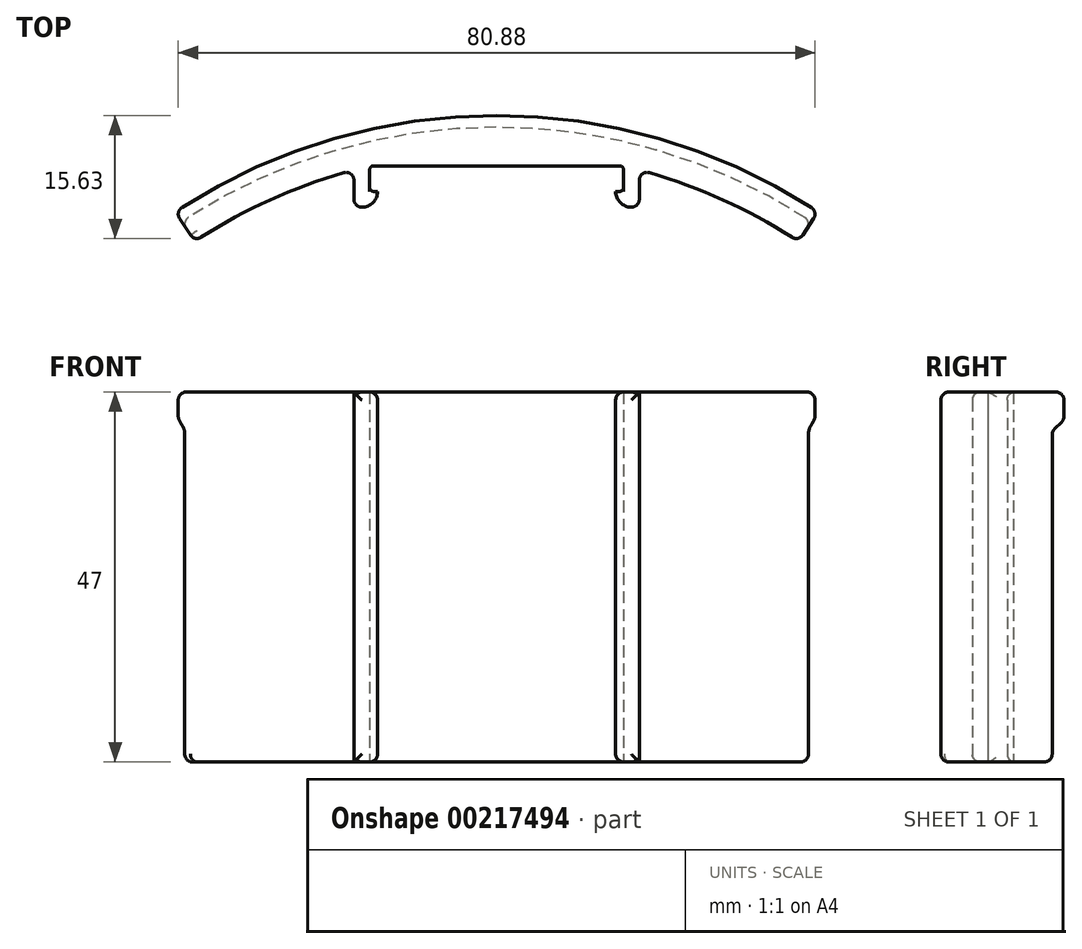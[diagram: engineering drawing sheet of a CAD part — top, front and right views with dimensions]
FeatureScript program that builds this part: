
annotation { "Feature Type Name" : "Feature", "Feature Type Description" : "" }
export const myFeature = defineFeature(function(context is Context, id is Id, definition is map)
    precondition{}
    {
        {
            var Q0;
            Q0=qCreatedBy(makeId("Top.planeOp"),FACE);
            var sketch = newSketch(context, id + "F0", { "sketchPlane" : qUnion([Q0])});
            skArc(sketch, "E0", {"start": v(40, 0) * mm, "mid": v(0, 12) * mm, "end": v(-40, 0) * mm});
            skPoint(sketch, "E1", {"position": v(0, 12) * mm});
            skArc(sketch, "E2.0", {"start": v(38.35, -2.5) * mm, "mid": v(0, 9) * mm, "end": v(-38.35, -2.5) * mm});
            skLineSegment(sketch, "E3", {"start": v(-40, 0) * mm, "end": v(-38.35, -2.5) * mm});
            skLineSegment(sketch, "E4", {"start": v(40, 0) * mm, "end": v(38.35, -2.5) * mm});
            skLineSegment(sketch, "E5", {"start": v(-16.12, 7.1) * mm, "end": v(16.12, 7.1) * mm});
            skLineSegment(sketch, "E6", {"start": v(-16.12, 7.1) * mm, "end": v(-16.12, 3.86) * mm});
            skLineSegment(sketch, "E7", {"start": v(-16.12, 3.86) * mm, "end": v(-15.12, 3.86) * mm});
            skLineSegment(sketch, "E8", {"start": v(-15.12, 3.86) * mm, "end": v(-15.12, 3.86) * mm});
            skLineSegment(sketch, "E9", {"start": v(-17.12, 1.86) * mm, "end": v(-18.13, 1.86) * mm});
            skLineSegment(sketch, "E10", {"start": v(-18.13, 1.86) * mm, "end": v(-18.13, 6.6) * mm});
            skLineSegment(sketch, "E11.MirrorCS", {"start": v(18.13, 1.86) * mm, "end": v(18.13, 6.6) * mm});
            skLineSegment(sketch, "E12.MirrorCS", {"start": v(16.12, 7.1) * mm, "end": v(16.12, 3.86) * mm});
            skLineSegment(sketch, "E13.MirrorCS", {"start": v(17.12, 1.86) * mm, "end": v(18.13, 1.86) * mm});
            skLineSegment(sketch, "E14.MirrorCS", {"start": v(16.12, 3.86) * mm, "end": v(15.12, 3.86) * mm});
            skLineSegment(sketch, "E15.MirrorCS", {"start": v(15.12, 3.86) * mm, "end": v(15.12, 3.86) * mm});
            skPoint(sketch, "E16.visualSharp", {"position": v(-15.12, 1.86) * mm});
            skArc(sketch, "E16.filletArc", {"start": v(-17.12, 1.86) * mm, "mid": v(-15.71, 2.44) * mm, "end": v(-15.13, 3.86) * mm});
            skPoint(sketch, "E17.visualSharp", {"position": v(15.12, 1.86) * mm});
            skArc(sketch, "E17.filletArc", {"start": v(15.13, 3.86) * mm, "mid": v(15.71, 2.44) * mm, "end": v(17.12, 1.86) * mm});
            skSolve(sketch);
        }
        {
            var Q0;
            Q0 = qSketchRegion(id + "F0", true);
            extrude(context, id + "F1", {"entities" : qUnion([Q0]), "endBound" : BoundingType.SYMMETRIC, "depth" : 47 * mm, "hasSecondDirection" : true, "secondDirectionOppositeDirection" : true, "secondDirectionDepth" : 25 * mm});
        }
        {
            var Q0;
            Q0=makeQuery(id+"F1.opExtrude","CAP_FACE",FACE,{"disambiguationData":[OSD([sQuery(id+"F0.wireOp",EDGE,"E0"),sQuery(id+"F0.wireOp",EDGE,"E2.0"),sQuery(id+"F0.wireOp",EDGE,"E3"),sQuery(id+"F0.wireOp",EDGE,"E4"),sQuery(id+"F0.wireOp",EDGE,"E5"),sQuery(id+"F0.wireOp",EDGE,"E6"),sQuery(id+"F0.wireOp",EDGE,"E7"),sQuery(id+"F0.wireOp",EDGE,"E8"),sQuery(id+"F0.wireOp",EDGE,"E9"),sQuery(id+"F0.wireOp",EDGE,"E10"),sQuery(id+"F0.wireOp",EDGE,"E11.MirrorCS"),sQuery(id+"F0.wireOp",EDGE,"E12.MirrorCS"),sQuery(id+"F0.wireOp",EDGE,"E13.MirrorCS"),sQuery(id+"F0.wireOp",EDGE,"E14.MirrorCS"),sQuery(id+"F0.wireOp",EDGE,"E15.MirrorCS")])],"isStart":false});
            var sketch = newSketch(context, id + "F2", { "sketchPlane" : qUnion([Q0])});
            skArc(sketch, "E18", {"start": v(38.35, -2.5) * mm, "mid": v(0, 9) * mm, "end": v(-38.35, -2.5) * mm});
            skArc(sketch, "E19.0", {"start": v(40.83, 1.25) * mm, "mid": v(0, 13.5) * mm, "end": v(-40.83, 1.25) * mm});
            skLineSegment(sketch, "E20", {"start": v(-40.83, 1.25) * mm, "end": v(-38.35, -2.5) * mm});
            skLineSegment(sketch, "E21", {"start": v(40.83, 1.25) * mm, "end": v(38.35, -2.5) * mm});
            skSolve(sketch);
        }
        {
            var Q0;
            Q0 = qSketchRegion(id + "F2", true);
            extrude(context, id + "F3", {"entities" : qUnion([Q0]), "operationType" : NewBodyOperationType.ADD, "oppositeDirection" : true, "depth" : 3.5 * mm});
        }
        {
            var Q0;
            Q0=makeQuery(id+"F1.opExtrude","SWEPT_EDGE",EDGE,{"disambiguationData":[OSD([sQuery(id+"F0.wireOp",EDGE,"E2.0"),sQuery(id+"F0.wireOp",EDGE,"E5"),sQuery(id+"F0.wireOp",EDGE,"E6")])]});
            var Q1;
            Q1=makeQuery(id+"F1.opExtrude","SWEPT_EDGE",EDGE,{"disambiguationData":[OSD([sQuery(id+"F0.wireOp",EDGE,"E6"),sQuery(id+"F0.wireOp",EDGE,"E7")])]});
            var Q2;
            Q2=makeQuery(id+"F1.opExtrude","SWEPT_EDGE",EDGE,{"disambiguationData":[OSD([sQuery(id+"F0.wireOp",EDGE,"E12.MirrorCS"),sQuery(id+"F0.wireOp",EDGE,"E14.MirrorCS")])]});
            var Q3;
            Q3=makeQuery(id+"F1.opExtrude","SWEPT_EDGE",EDGE,{"disambiguationData":[OSD([sQuery(id+"F0.wireOp",EDGE,"E2.0"),sQuery(id+"F0.wireOp",EDGE,"E5"),sQuery(id+"F0.wireOp",EDGE,"E12.MirrorCS")])]});
            fillet(context, id + "F4", {"entities" : qUnion([Q0, Q1, Q2, Q3]), "radius" : .5 * mm, "tangentPropagation" : true, "allowEdgeOverflow" : false});
        }
        {
            var Q0;
            Q0=makeQuery(id+"FpLEZJu2neVifi9_1.1.F3.boolean.opBoolean","INTERSECT",EDGE,{"derivedFrom":[makeQuery(id+"F1.opExtrude","SWEPT_FACE",FACE,{"disambiguationData":[OSD([sQuery(id+"F0.wireOp",EDGE,"E0")])]}),makeQuery(id+"FpLEZJu2neVifi9_1.1.F3.opExtrude","CAP_FACE",FACE,{"disambiguationData":[OSD([sQuery(id+"F2.wireOp",EDGE,"E18"),sQuery(id+"F2.wireOp",EDGE,"E19.0"),sQuery(id+"F2.wireOp",EDGE,"E20"),sQuery(id+"F2.wireOp",EDGE,"E21")])],"isStart":false})]});
            var Q1;
            Q1=makeQuery(id+"F3.boolean.opBoolean","INTERSECT",EDGE,{"derivedFrom":[makeQuery(id+"F1.opExtrude","SWEPT_FACE",FACE,{"disambiguationData":[OSD([sQuery(id+"F0.wireOp",EDGE,"E0")])]}),makeQuery(id+"F3.opExtrude","CAP_FACE",FACE,{"disambiguationData":[OSD([sQuery(id+"F2.wireOp",EDGE,"E18"),sQuery(id+"F2.wireOp",EDGE,"E19.0"),sQuery(id+"F2.wireOp",EDGE,"E20"),sQuery(id+"F2.wireOp",EDGE,"E21")])],"isStart":false})]});
            chamfer(context, id + "F5", {"entities" : qUnion([Q0, Q1]), "width" : 1.5 * mm, "tangentPropagation" : true});
        }
        {
            var Q0;
            Q0=makeQuery(id+"FpLEZJu2neVifi9_1.1.F3.opExtrude","SWEPT_FACE",FACE,{"disambiguationData":[OSD([sQuery(id+"F2.wireOp",EDGE,"E19.0")])]});
            var Q1;
            Q1=makeQuery(id+"F3.opExtrude","SWEPT_FACE",FACE,{"disambiguationData":[OSD([sQuery(id+"F2.wireOp",EDGE,"E19.0")])]});
            var Q2;
            {var subQ0=sQuery(id+"F2.wireOp",EDGE,"E20");Q2=makeQuery(id+"FpLEZJu2neVifi9_1.1.F3.boolean.opBoolean","MERGE",FACE,{"derivedFrom":[makeQuery(id+"F3.boolean.opBoolean","MERGE",FACE,{"derivedFrom":[makeQuery(id+"F1.opExtrude","SWEPT_FACE",FACE,{"disambiguationData":[OSD([sQuery(id+"F0.wireOp",EDGE,"E3")])]}),makeQuery(id+"F3.opExtrude","SWEPT_FACE",FACE,{"disambiguationData":[OSD([subQ0])]})]}),makeQuery(id+"FpLEZJu2neVifi9_1.1.F3.opExtrude","SWEPT_FACE",FACE,{"disambiguationData":[OSD([subQ0])]})]});}
            var Q3;
            {var subQ0=sQuery(id+"F2.wireOp",EDGE,"E21");Q3=makeQuery(id+"FpLEZJu2neVifi9_1.1.F3.boolean.opBoolean","MERGE",FACE,{"derivedFrom":[makeQuery(id+"F3.boolean.opBoolean","MERGE",FACE,{"derivedFrom":[makeQuery(id+"F1.opExtrude","SWEPT_FACE",FACE,{"disambiguationData":[OSD([sQuery(id+"F0.wireOp",EDGE,"E4")])]}),makeQuery(id+"F3.opExtrude","SWEPT_FACE",FACE,{"disambiguationData":[OSD([subQ0])]})]}),makeQuery(id+"FpLEZJu2neVifi9_1.1.F3.opExtrude","SWEPT_FACE",FACE,{"disambiguationData":[OSD([subQ0])]})]});}
            var Q4;
            {var subQ0=sQuery(id+"F0.wireOp",EDGE,"E2.0");Q4=makeQuery(id+"F1.opExtrude","SWEPT_FACE",FACE,{"disambiguationData":[OSD([subQ0]),TDD([makeQuery(id+"F0.imprint","IMPRINT",EDGE,{"disambiguationData":[TD([[makeQuery(id+"F0.imprint","INTERSECT",VERTEX,{"derivedFrom":[subQ0,sQuery(id+"F0.wireOp",EDGE,"E4")]}),-1.0]])],"derivedFrom":subQ0})])]});}
            var Q5;
            {var subQ0=sQuery(id+"F0.wireOp",EDGE,"E2.0");Q5=makeQuery(id+"F1.opExtrude","SWEPT_FACE",FACE,{"disambiguationData":[OSD([subQ0]),TDD([makeQuery(id+"F0.imprint","IMPRINT",EDGE,{"disambiguationData":[TD([[makeQuery(id+"F0.imprint","INTERSECT",VERTEX,{"derivedFrom":[subQ0,sQuery(id+"F0.wireOp",EDGE,"E3")]}),1.0]])],"derivedFrom":subQ0})])]});}
            var Q6;
            Q6=makeQuery(id+"F1.opExtrude","SWEPT_FACE",FACE,{"disambiguationData":[OSD([sQuery(id+"F0.wireOp",EDGE,"E9")])]});
            var Q7;
            Q7=makeQuery(id+"F1.opExtrude","SWEPT_FACE",FACE,{"disambiguationData":[OSD([sQuery(id+"F0.wireOp",EDGE,"E13.MirrorCS")])]});
            var Q8;
            Q8=makeQuery(id+"F1.opExtrude","SWEPT_FACE",FACE,{"disambiguationData":[OSD([sQuery(id+"F0.wireOp",EDGE,"E0")])]});
            fillet(context, id + "F6", {"entities" : qUnion([Q0, Q1, Q2, Q3, Q4, Q5, Q6, Q7, Q8]), "radius" : 1 * mm, "tangentPropagation" : true, "allowEdgeOverflow" : false});
        }
    });
